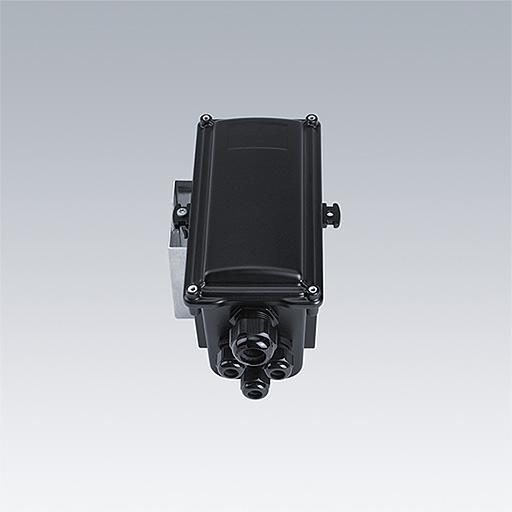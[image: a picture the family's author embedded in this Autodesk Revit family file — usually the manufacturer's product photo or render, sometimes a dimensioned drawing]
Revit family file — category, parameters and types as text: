
# Revit family: Zumtobel ALTIS GEN5 1 Module
name_source: partatom
category: Lighting Fixtures
units: mm (PartAtom-declared; Revit-internal decimal feet)

## family parameters
Cut with Voids When Loaded = No
Host = Face
Light Source = No
Maintain Annotation Orientation = No
Part Type = Normal
Room Calculation Point = Yes
Round Connector Dimension = Use Diameter
Shared = No

## types (1)
- Zumtobel ALTIS GEN5 1 Module
    1 Module = Yes
    1 Module Standalone = No
    Apparent Load = 457 VA
    Assembly Code = Pr_70_70_48_31
    Default Elevation = 0 mm  [stored 0 ft]
    Description = Sports Floodlighting
    Export Type to IFC As = IfcLightFixtureType
    Gearbox = No
    Initial Color Temperature = 4000 K
    Junction Box = No
    Lamp = LED
    Luminaire Height = 369 mm
    Luminaire Length = 170 mm  [stored 0.557743 ft]
    Luminaire Width = 675 mm  [stored 2.21457 ft]
    Manufacturer = Zumtobel Lighting
    Material = Thorn-Aluminium-RAL 7043-Traffic Grey B
    Model = 96671918
    Power Factor = 1
    Power Supply Support = No
    RGB Light Colours = No
    SELECT ACCESSORIES = SELECT CONNECTION BOX POSITION
    SELECT MODULE PROPERTIES = SELECT INSTALLATION PROPERTIES
    Type Gearbox = Thorn ALTIS GEN5 Gearbox-Premium-class C5 with NTC : ALG5 GB 1368W 0.70A 565V 2CH DA
    Type IFC Predefined Type = DIRECTIONSOURCE
    Type Image = TLG_ALT5_F_V1_FIFA.jpg
    Type Junction Box = Thorn ALTIS GEN5 Junction Box : ALG5 JUNCTION BOX GB TO 3X1 MODULE
    URL = https://www.thornlighting.com
    Visibility Connection Box = No
    Visibility Gearbox = No
    Visibility Support = No
    Wattage = 457 W

note: [stored X ft] marks values corroborated as IEEE doubles in the binary element streams (Revit-internal decimal feet)

## geometry (parser evidence)
native form markers: Sweep x14
no freeform markers — native parametric forms only
